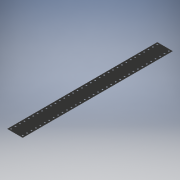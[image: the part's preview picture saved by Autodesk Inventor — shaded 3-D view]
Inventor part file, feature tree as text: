
AUTODESK INVENTOR PART (.ipt)
format: ipt  version: 2019 (Build 230136000, 136)  size: 195,584 bytes
history: native  units: mm
features: extrude x1, other x1
ambient origin geometry x8: Origin, YZ Plane, XZ Plane, XY Plane, X Axis, Y Axis, Z Axis, Center Point
bodies: Body1 (feature_tree)
feature tree (2):
  extrude  "Foam Body"  Depth=1859.0mm
  other  "Foam Scheme"
